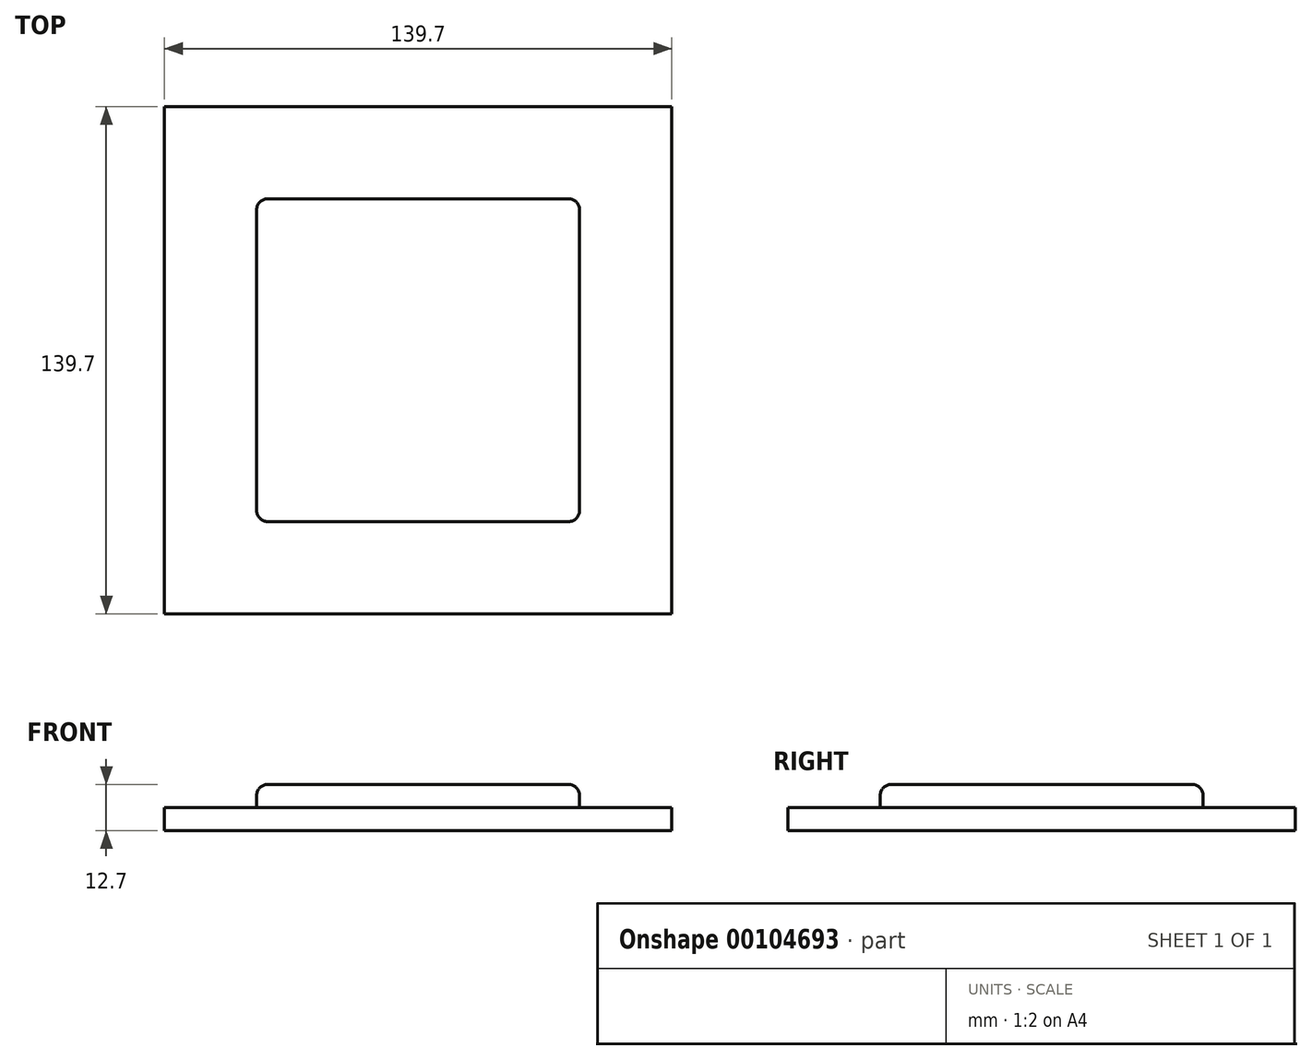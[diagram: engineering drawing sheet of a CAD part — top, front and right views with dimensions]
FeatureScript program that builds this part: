
annotation { "Feature Type Name" : "Feature", "Feature Type Description" : "" }
export const myFeature = defineFeature(function(context is Context, id is Id, definition is map)
    precondition{}
    {
        {
            var Q0;
            Q0=qCreatedBy(makeId("Top.planeOp"),FACE);
            var sketch = newSketch(context, id + "F0", { "sketchPlane" : qUnion([Q0])});
            skLineSegment(sketch, "E0.bottom", {"start": v(-93.7, 70.88) * mm, "end": v(46, 70.88) * mm});
            skLineSegment(sketch, "E0.top", {"start": v(-93.7, -68.82) * mm, "end": v(46, -68.82) * mm});
            skLineSegment(sketch, "E0.left", {"start": v(-93.7, 70.88) * mm, "end": v(-93.7, -68.82) * mm});
            skLineSegment(sketch, "E0.right", {"start": v(46, 70.88) * mm, "end": v(46, -68.82) * mm});
            skLineSegment(sketch, "E1.bottom", {"start": v(-68.3, 45.48) * mm, "end": v(20.6, 45.48) * mm});
            skLineSegment(sketch, "E1.top", {"start": v(-68.3, -43.42) * mm, "end": v(20.6, -43.42) * mm});
            skLineSegment(sketch, "E1.left", {"start": v(-68.3, 45.48) * mm, "end": v(-68.3, -43.42) * mm});
            skLineSegment(sketch, "E1.right", {"start": v(20.6, 45.48) * mm, "end": v(20.6, -43.42) * mm});
            skSolve(sketch);
        }
        {
            var Q0;
            Q0=makeQuery(id+"F0.imprint","IMPRINT",FACE,{"disambiguationData":[TD([[makeQuery(id+"F0.imprint","IMPRINT",EDGE,{"derivedFrom":sQuery(id+"F0.wireOp",EDGE,"E1.bottom")}),-1.0]])]});
            extrude(context, id + "F1", {"entities" : qUnion([Q0]), "depth" : 12.7 * mm});
        }
        {
            var Q0;
            Q0 = qSketchRegion(id + "F0", true);
            extrude(context, id + "F2", {"entities" : qUnion([Q0]), "operationType" : NewBodyOperationType.ADD, "depth" : 6.4 * mm});
        }
        {
            var Q0;
            Q0=makeQuery(id+"F1.opExtrude","CAP_EDGE",EDGE,{"disambiguationData":[OSD([sQuery(id+"F0.wireOp",EDGE,"E1.left")])],"isStart":false});
            var Q1;
            Q1=makeQuery(id+"F1.opExtrude","CAP_EDGE",EDGE,{"disambiguationData":[OSD([sQuery(id+"F0.wireOp",EDGE,"E1.top")])],"isStart":false});
            var Q2;
            Q2=makeQuery(id+"F1.opExtrude","CAP_EDGE",EDGE,{"disambiguationData":[OSD([sQuery(id+"F0.wireOp",EDGE,"E1.right")])],"isStart":false});
            var Q3;
            Q3=makeQuery(id+"F1.opExtrude","CAP_EDGE",EDGE,{"disambiguationData":[OSD([sQuery(id+"F0.wireOp",EDGE,"E1.bottom")])],"isStart":false});
            var Q4;
            Q4=makeQuery(id+"F1.opExtrude","SWEPT_EDGE",EDGE,{"disambiguationData":[OSD([sQuery(id+"F0.wireOp",EDGE,"E1.top"),sQuery(id+"F0.wireOp",EDGE,"E1.right")])]});
            var Q5;
            Q5=makeQuery(id+"F1.opExtrude","SWEPT_EDGE",EDGE,{"disambiguationData":[OSD([sQuery(id+"F0.wireOp",EDGE,"E1.top"),sQuery(id+"F0.wireOp",EDGE,"E1.left")])]});
            var Q6;
            Q6=makeQuery(id+"F1.opExtrude","SWEPT_EDGE",EDGE,{"disambiguationData":[OSD([sQuery(id+"F0.wireOp",EDGE,"E1.bottom"),sQuery(id+"F0.wireOp",EDGE,"E1.left")])]});
            var Q7;
            Q7=makeQuery(id+"F1.opExtrude","SWEPT_EDGE",EDGE,{"disambiguationData":[OSD([sQuery(id+"F0.wireOp",EDGE,"E1.bottom"),sQuery(id+"F0.wireOp",EDGE,"E1.right")])]});
            fillet(context, id + "F3", {"entities" : qUnion([Q0, Q1, Q2, Q3, Q4, Q5, Q6, Q7]), "radius" : 3 * mm, "tangentPropagation" : true, "allowEdgeOverflow" : false});
        }
    });
